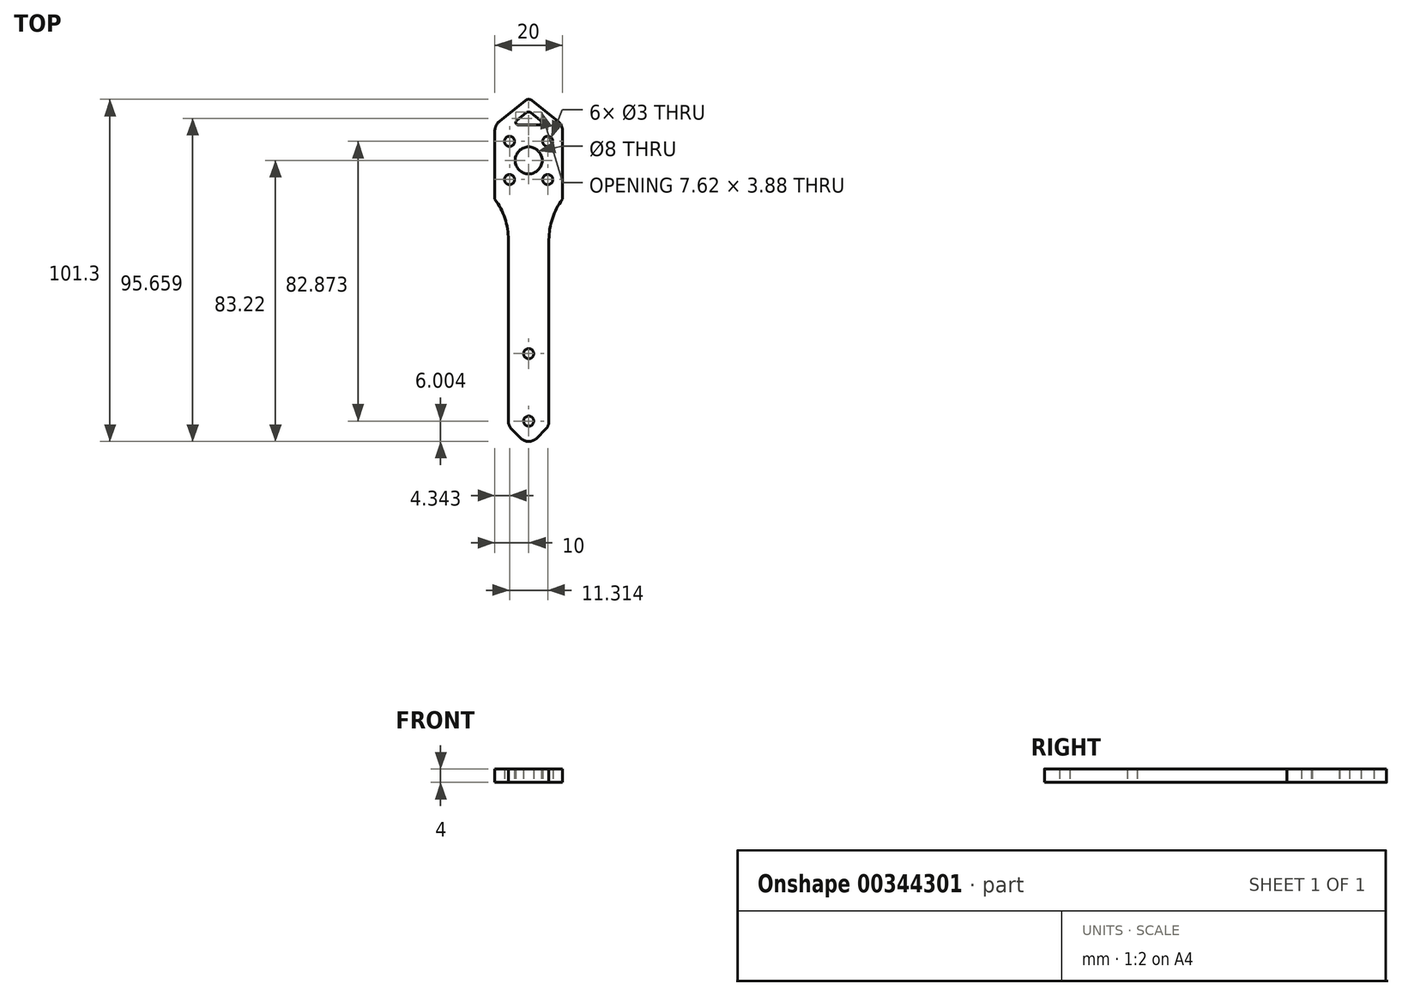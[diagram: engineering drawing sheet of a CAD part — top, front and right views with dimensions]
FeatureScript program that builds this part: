
annotation { "Feature Type Name" : "Feature", "Feature Type Description" : "" }
export const myFeature = defineFeature(function(context is Context, id is Id, definition is map)
    precondition{}
    {
        {
            var Q0;
            Q0=qCreatedBy(makeId("Top.planeOp"),FACE);
            var sketch = newSketch(context, id + "F0", { "sketchPlane" : qUnion([Q0])});
            skLineSegment(sketch, "E0", {"start": v(0, 72.7) * mm, "end": v(0, -98.78) * mm, "construction": true});
            skLineSegment(sketch, "E1.0", {"start": v(6, -23.5) * mm, "end": v(6, -77.22) * mm});
            skCircle(sketch, "E2", {"center": v(0, 0) * mm, "radius": 4 * mm});
            skLineSegment(sketch, "E3.0", {"start": v(10, 8.82) * mm, "end": v(10, -11.5) * mm});
            skCircle(sketch, "E4", {"center": v(0, 0) * mm, "radius": 8 * mm, "construction": true});
            skLineSegment(sketch, "E5", {"start": v(0, 0) * mm, "end": v(-5.66, 5.66) * mm, "construction": true});
            skCircle(sketch, "E6", {"center": v(-5.66, 5.66) * mm, "radius": 1.5 * mm});
            skLineSegment(sketch, "E7", {"start": v(0.94, 17.75) * mm, "end": v(8.69, 11.55) * mm});
            skArc(sketch, "E8", {"start": v(10, -11.5) * mm, "mid": v(7.03, -17.18) * mm, "end": v(6, -23.5) * mm});
            skCircle(sketch, "E9.1.0", {"center": v(-5.66, -5.66) * mm, "radius": 1.5 * mm});
            skCircle(sketch, "E9.2.0", {"center": v(5.66, -5.66) * mm, "radius": 1.5 * mm});
            skCircle(sketch, "E10.1.3.0", {"center": v(5.66, 5.66) * mm, "radius": 1.5 * mm});
            skLineSegment(sketch, "E11", {"start": v(0, 10.5) * mm, "end": v(3.06, 10.5) * mm});
            skLineSegment(sketch, "E12", {"start": v(3.53, 11.84) * mm, "end": v(0.62, 14.16) * mm});
            skCircle(sketch, "E13", {"center": v(0, -57.22) * mm, "radius": 1.5 * mm});
            skCircle(sketch, "E14", {"center": v(0, -77.22) * mm, "radius": 1.5 * mm});
            skLineSegment(sketch, "E15", {"start": v(0, 0) * mm, "end": v(49.4, -49.4) * mm, "construction": true});
            skLineSegment(sketch, "E16", {"start": v(49.4, -49.4) * mm, "end": v(0, -98.78) * mm, "construction": true});
            skLineSegment(sketch, "E17", {"start": v(0, -77.22) * mm, "end": v(10.78, -88) * mm, "construction": true});
            skLineSegment(sketch, "E18", {"start": v(4.97, -79.7) * mm, "end": v(2.47, -82.2) * mm});
            skArc(sketch, "E19", {"start": v(0, -83.22) * mm, "mid": v(1.34, -82.95) * mm, "end": v(2.47, -82.2) * mm});
            skPoint(sketch, "E20", {"position": v(0, -83.22) * mm});
            skArc(sketch, "E21.filletArc", {"start": v(4.97, -79.7) * mm, "mid": v(5.73, -78.56) * mm, "end": v(6, -77.22) * mm});
            skArc(sketch, "E22.MirrorCS", {"start": v(0, -83.22) * mm, "mid": v(-1.34, -82.95) * mm, "end": v(-2.47, -82.2) * mm});
            skLineSegment(sketch, "E23.MirrorCS", {"start": v(-4.97, -79.7) * mm, "end": v(-2.47, -82.2) * mm});
            skArc(sketch, "E24.MirrorCS", {"start": v(-4.97, -79.7) * mm, "mid": v(-5.73, -78.56) * mm, "end": v(-6, -77.22) * mm});
            skLineSegment(sketch, "E25.MirrorCS", {"start": v(-6, -23.5) * mm, "end": v(-6, -77.22) * mm});
            skArc(sketch, "E26.MirrorCS", {"start": v(-10, -11.5) * mm, "mid": v(-7.03, -17.18) * mm, "end": v(-6, -23.5) * mm});
            skLineSegment(sketch, "E27.MirrorCS", {"start": v(-10, 8.82) * mm, "end": v(-10, -11.5) * mm});
            skLineSegment(sketch, "E28.MirrorCS", {"start": v(-0.94, 17.75) * mm, "end": v(-8.69, 11.55) * mm});
            skLineSegment(sketch, "E29.MirrorCS", {"start": v(-3.53, 11.84) * mm, "end": v(-0.62, 14.16) * mm});
            skLineSegment(sketch, "E30.MirrorCS", {"start": v(0, 10.5) * mm, "end": v(-3.06, 10.5) * mm});
            skPoint(sketch, "E31.visualSharp", {"position": v(-5.2, 10.5) * mm});
            skArc(sketch, "E31.filletArc", {"start": v(-3.53, 11.84) * mm, "mid": v(-3.77, 11) * mm, "end": v(-3.06, 10.5) * mm});
            skPoint(sketch, "E32.visualSharp", {"position": v(5.2, 10.5) * mm});
            skArc(sketch, "E32.filletArc", {"start": v(3.06, 10.5) * mm, "mid": v(3.77, 11) * mm, "end": v(3.53, 11.84) * mm});
            skPoint(sketch, "E33.visualSharp", {"position": v(0, 14.66) * mm});
            skArc(sketch, "E33.filletArc", {"start": v(0.62, 14.16) * mm, "mid": v(0, 14.38) * mm, "end": v(-0.62, 14.16) * mm});
            skPoint(sketch, "E34.visualSharp", {"position": v(0, 18.5) * mm});
            skArc(sketch, "E34.filletArc", {"start": v(0.94, 17.75) * mm, "mid": v(0, 18.08) * mm, "end": v(-0.94, 17.75) * mm});
            skPoint(sketch, "E35.visualSharp", {"position": v(10, 10.5) * mm});
            skArc(sketch, "E35.filletArc", {"start": v(10, 8.82) * mm, "mid": v(9.65, 10.33) * mm, "end": v(8.69, 11.55) * mm});
            skPoint(sketch, "E36.visualSharp", {"position": v(-10, 10.5) * mm});
            skArc(sketch, "E36.filletArc", {"start": v(-8.69, 11.55) * mm, "mid": v(-9.65, 10.33) * mm, "end": v(-10, 8.82) * mm});
            skSolve(sketch);
        }
        {
            var Q0;
            Q0=makeQuery(id+"F0.imprint","IMPRINT",FACE,{"disambiguationData":[TD([[makeQuery(id+"F0.imprint","IMPRINT",EDGE,{"derivedFrom":sQuery(id+"F0.wireOp",EDGE,"E1.0")}),-1.0]])]});
            extrude(context, id + "F1", {"entities" : qUnion([Q0]), "depth" : 4 * mm});
        }
    });
